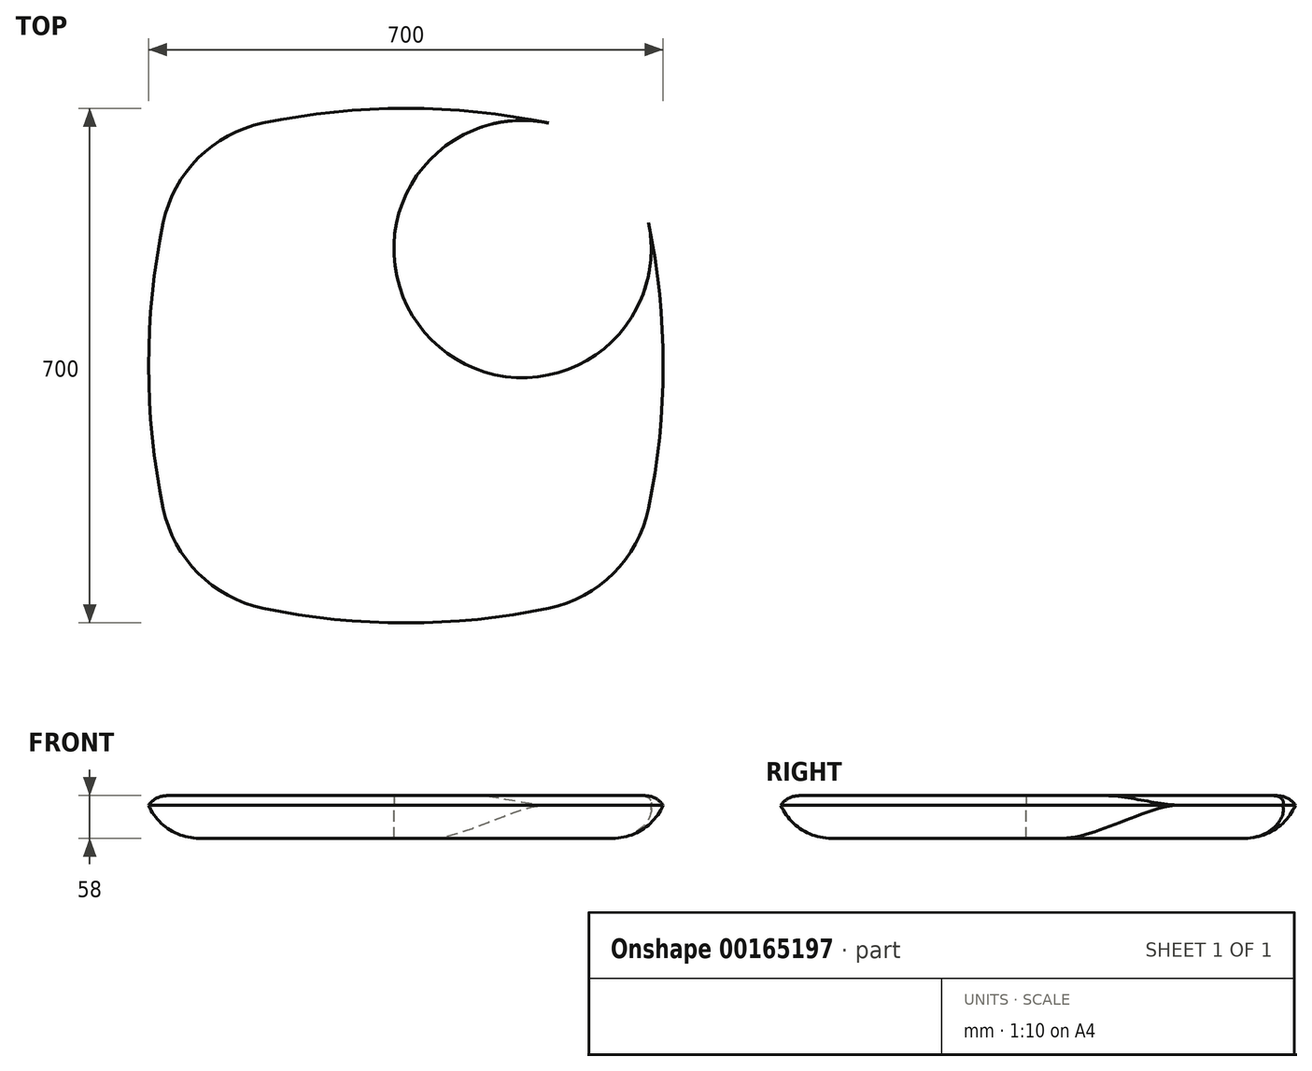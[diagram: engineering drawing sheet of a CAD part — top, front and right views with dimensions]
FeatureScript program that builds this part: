
annotation { "Feature Type Name" : "Feature", "Feature Type Description" : "" }
export const myFeature = defineFeature(function(context is Context, id is Id, definition is map)
    precondition{}
    {
        {
            var Q0;
            Q0=qCreatedBy(makeId("Top.planeOp"),FACE);
            var sketch = newSketch(context, id + "F0", { "sketchPlane" : qUnion([Q0])});
            skLineSegment(sketch, "E0.bottom", {"start": v(301.28, -301.28) * mm, "end": v(-301.28, -301.28) * mm, "construction": true});
            skLineSegment(sketch, "E0.top", {"start": v(301.28, 301.28) * mm, "end": v(-301.28, 301.28) * mm, "construction": true});
            skLineSegment(sketch, "E0.left", {"start": v(301.28, -301.28) * mm, "end": v(301.28, 301.28) * mm, "construction": true});
            skLineSegment(sketch, "E0.right", {"start": v(-301.28, -301.28) * mm, "end": v(-301.28, 301.28) * mm, "construction": true});
            skPoint(sketch, "E0.middle", {"position": v(0, 0) * mm});
            skArc(sketch, "E1", {"start": v(301.28, 301.28) * mm, "mid": v(0, 350) * mm, "end": v(-301.28, 301.28) * mm});
            skArc(sketch, "E2", {"start": v(-301.28, 301.28) * mm, "mid": v(-350, 0) * mm, "end": v(-301.28, -301.28) * mm});
            skArc(sketch, "E3", {"start": v(-301.28, -301.28) * mm, "mid": v(0, -350) * mm, "end": v(301.28, -301.28) * mm});
            skArc(sketch, "E4", {"start": v(301.28, -301.28) * mm, "mid": v(350, 0) * mm, "end": v(301.28, 301.28) * mm});
            skCircle(sketch, "E5", {"center": v(-158.7, -158.7) * mm, "radius": 175 * mm});
            skLineSegment(sketch, "E6", {"start": v(-301.28, 301.28) * mm, "end": v(301.28, -301.28) * mm, "construction": true});
            skLineSegment(sketch, "E7", {"start": v(-282.21, 0) * mm, "end": v(273.2, 0) * mm, "construction": true});
            skCircle(sketch, "E8.MirrorC", {"center": v(158.7, 158.7) * mm, "radius": 175 * mm});
            skCircle(sketch, "E9.MirrorC", {"center": v(-158.7, 158.7) * mm, "radius": 175 * mm});
            skCircle(sketch, "E10.MirrorC", {"center": v(158.7, -158.7) * mm, "radius": 175 * mm});
            skSolve(sketch);
        }
        {
            var Q0;
            {var subQ0=sQuery(id+"F0.wireOp",EDGE,"E5");var subQ1=makeQuery(id+"F0.imprint","INTERSECT",VERTEX,{"derivedFrom":[sQuery(id+"F0.wireOp",EDGE,"E2"),subQ0]});Q0=makeQuery(id+"F0.imprint","IMPRINT",FACE,{"disambiguationData":[TD([[makeQuery(id+"F0.imprint","IMPRINT",EDGE,{"disambiguationData":[TD([[subQ1,-1.0]])],"derivedFrom":subQ0}),1.0]])]});}
            var Q1;
            {var subQ3=sQuery(id+"F0.wireOp",EDGE,"E8.MirrorC");var subQ13=sQuery(id+"F0.wireOp",EDGE,"E1");var subQ14=makeQuery(id+"F0.imprint","INTERSECT",VERTEX,{"derivedFrom":[subQ13,subQ3]});Q1=makeQuery(id+"F0.imprint","IMPRINT",FACE,{"disambiguationData":[TD([[makeQuery(id+"F0.imprint","IMPRINT",EDGE,{"disambiguationData":[TD([[subQ14,-1.0]])],"derivedFrom":subQ13}),1.0]])]});}
            var Q2;
            {var subQ0=sQuery(id+"F0.wireOp",EDGE,"E10.MirrorC");var subQ1=makeQuery(id+"F0.imprint","INTERSECT",VERTEX,{"derivedFrom":[sQuery(id+"F0.wireOp",EDGE,"E3"),subQ0]});Q2=makeQuery(id+"F0.imprint","IMPRINT",FACE,{"disambiguationData":[TD([[makeQuery(id+"F0.imprint","IMPRINT",EDGE,{"disambiguationData":[TD([[subQ1,-1.0]])],"derivedFrom":subQ0}),1.0]])]});}
            var Q3;
            {var subQ0=sQuery(id+"F0.wireOp",EDGE,"E5");var subQ1=sQuery(id+"F0.wireOp",EDGE,"E3");var subQ2=makeQuery(id+"F0.imprint","INTERSECT",VERTEX,{"derivedFrom":[subQ1,subQ0]});Q3=makeQuery(id+"F0.imprint","IMPRINT",FACE,{"disambiguationData":[TD([[makeQuery(id+"F0.imprint","IMPRINT",EDGE,{"disambiguationData":[TD([[subQ2,-1.0]])],"derivedFrom":subQ1}),1.0]])]});}
            var Q4;
            {var subQ0=sQuery(id+"F0.wireOp",EDGE,"E9.MirrorC");var subQ1=sQuery(id+"F0.wireOp",EDGE,"E2");var subQ2=makeQuery(id+"F0.imprint","INTERSECT",VERTEX,{"derivedFrom":[subQ1,subQ0]});Q4=makeQuery(id+"F0.imprint","IMPRINT",FACE,{"disambiguationData":[TD([[makeQuery(id+"F0.imprint","IMPRINT",EDGE,{"disambiguationData":[TD([[subQ2,-1.0]])],"derivedFrom":subQ1}),1.0]])]});}
            var Q5;
            {var subQ0=sQuery(id+"F0.wireOp",EDGE,"E9.MirrorC");var subQ1=sQuery(id+"F0.wireOp",EDGE,"E5");var subQ2=makeQuery(id+"F0.imprint","INTERSECT",VERTEX,{"disambiguationData":[OD(0.0)],"derivedFrom":[subQ1,subQ0]});Q5=makeQuery(id+"F0.imprint","IMPRINT",FACE,{"disambiguationData":[TD([[makeQuery(id+"F0.imprint","IMPRINT",EDGE,{"disambiguationData":[TD([[subQ2,-1.0]])],"derivedFrom":subQ1}),1.0]])]});}
            var Q6;
            {var subQ0=sQuery(id+"F0.wireOp",EDGE,"E9.MirrorC");var subQ2=sQuery(id+"F0.wireOp",EDGE,"E5");var subQ4=makeQuery(id+"F0.imprint","INTERSECT",VERTEX,{"disambiguationData":[OD(0.0)],"derivedFrom":[subQ2,subQ0]});Q6=makeQuery(id+"F0.imprint","IMPRINT",FACE,{"disambiguationData":[TD([[makeQuery(id+"F0.imprint","IMPRINT",EDGE,{"disambiguationData":[TD([[subQ4,-1.0]])],"derivedFrom":subQ2}),-1.0]])]});}
            var Q7;
            {var subQ0=sQuery(id+"F0.wireOp",EDGE,"E9.MirrorC");var subQ1=sQuery(id+"F0.wireOp",EDGE,"E5");var subQ2=makeQuery(id+"F0.imprint","INTERSECT",VERTEX,{"disambiguationData":[OD(0.0)],"derivedFrom":[subQ1,subQ0]});Q7=makeQuery(id+"F0.imprint","IMPRINT",FACE,{"disambiguationData":[TD([[makeQuery(id+"F0.imprint","IMPRINT",EDGE,{"disambiguationData":[TD([[subQ2,1.0]])],"derivedFrom":subQ1}),-1.0]])]});}
            var Q8;
            {var subQ0=sQuery(id+"F0.wireOp",EDGE,"E8.MirrorC");var subQ4=sQuery(id+"F0.wireOp",EDGE,"E9.MirrorC");var subQ5=makeQuery(id+"F0.imprint","INTERSECT",VERTEX,{"disambiguationData":[OD(0.0)],"derivedFrom":[subQ0,subQ4]});Q8=makeQuery(id+"F0.imprint","IMPRINT",FACE,{"disambiguationData":[TD([[makeQuery(id+"F0.imprint","IMPRINT",EDGE,{"disambiguationData":[TD([[subQ5,1.0]])],"derivedFrom":subQ0}),-1.0]])]});}
            var Q9;
            {var subQ0=sQuery(id+"F0.wireOp",EDGE,"E10.MirrorC");var subQ1=sQuery(id+"F0.wireOp",EDGE,"E8.MirrorC");var subQ2=makeQuery(id+"F0.imprint","INTERSECT",VERTEX,{"disambiguationData":[OD(0.0)],"derivedFrom":[subQ1,subQ0]});Q9=makeQuery(id+"F0.imprint","IMPRINT",FACE,{"disambiguationData":[TD([[makeQuery(id+"F0.imprint","IMPRINT",EDGE,{"disambiguationData":[TD([[subQ2,1.0]])],"derivedFrom":subQ1}),-1.0]])]});}
            var Q10;
            {var subQ0=sQuery(id+"F0.wireOp",EDGE,"E10.MirrorC");var subQ1=sQuery(id+"F0.wireOp",EDGE,"E4");var subQ2=makeQuery(id+"F0.imprint","INTERSECT",VERTEX,{"derivedFrom":[subQ1,subQ0]});Q10=makeQuery(id+"F0.imprint","IMPRINT",FACE,{"disambiguationData":[TD([[makeQuery(id+"F0.imprint","IMPRINT",EDGE,{"disambiguationData":[TD([[subQ2,-1.0]])],"derivedFrom":subQ1}),1.0]])]});}
            var Q11;
            {var subQ0=sQuery(id+"F0.wireOp",EDGE,"E10.MirrorC");var subQ1=sQuery(id+"F0.wireOp",EDGE,"E5");var subQ2=makeQuery(id+"F0.imprint","INTERSECT",VERTEX,{"disambiguationData":[OD(0.0)],"derivedFrom":[subQ1,subQ0]});Q11=makeQuery(id+"F0.imprint","IMPRINT",FACE,{"disambiguationData":[TD([[makeQuery(id+"F0.imprint","IMPRINT",EDGE,{"disambiguationData":[TD([[subQ2,1.0]])],"derivedFrom":subQ1}),1.0]])]});}
            var Q12;
            {var subQ0=sQuery(id+"F0.wireOp",EDGE,"E9.MirrorC");var subQ1=sQuery(id+"F0.wireOp",EDGE,"E8.MirrorC");var subQ2=makeQuery(id+"F0.imprint","INTERSECT",VERTEX,{"disambiguationData":[OD(0.0)],"derivedFrom":[subQ1,subQ0]});Q12=makeQuery(id+"F0.imprint","IMPRINT",FACE,{"disambiguationData":[TD([[makeQuery(id+"F0.imprint","IMPRINT",EDGE,{"disambiguationData":[TD([[subQ2,-1.0]])],"derivedFrom":subQ1}),-1.0]])]});}
            extrude(context, id + "F1", {"entities" : qUnion([Q0, Q1, Q2, Q3, Q4, Q5, Q6, Q7, Q8, Q9, Q10, Q11, Q12]), "depth" : 13 * mm});
        }
        {
            var Q0;
            Q0=makeQuery(id+"F1.opExtrude","CAP_EDGE",EDGE,{"disambiguationData":[OSD([sQuery(id+"F0.wireOp",EDGE,"E3")])],"isStart":false});
            fillet(context, id + "F2", {"entities" : qUnion([Q0]), "radius" : 30.5 * mm, "tangentPropagation" : true, "allowEdgeOverflow" : false});
        }
        {
            var Q0;
            Q0=makeQuery(id+"F1.opExtrude","CAP_FACE",FACE,{"disambiguationData":[OSD([sQuery(id+"F0.wireOp",EDGE,"E1"),sQuery(id+"F0.wireOp",EDGE,"E2"),sQuery(id+"F0.wireOp",EDGE,"E3"),sQuery(id+"F0.wireOp",EDGE,"E4"),sQuery(id+"F0.wireOp",EDGE,"E5"),sQuery(id+"F0.wireOp",EDGE,"E8.MirrorC"),sQuery(id+"F0.wireOp",EDGE,"E9.MirrorC"),sQuery(id+"F0.wireOp",EDGE,"E10.MirrorC")])],"isStart":true});
            extrude(context, id + "F3", {"entities" : qUnion([Q0]), "depth" : 45 * mm});
        }
        {
            var Q0;
            {var subQ0=sQuery(id+"F0.wireOp",EDGE,"E10.MirrorC");var subQ1=sQuery(id+"F0.wireOp",EDGE,"E9.MirrorC");var subQ2=sQuery(id+"F0.wireOp",EDGE,"E8.MirrorC");var subQ3=sQuery(id+"F0.wireOp",EDGE,"E5");var subQ4=sQuery(id+"F0.wireOp",EDGE,"E4");var subQ5=sQuery(id+"F0.wireOp",EDGE,"E3");var subQ6=sQuery(id+"F0.wireOp",EDGE,"E2");var subQ7=sQuery(id+"F0.wireOp",EDGE,"E1");Q0=makeQuery(id+"F3.opExtrude","CAP_EDGE",EDGE,{"disambiguationData":[OSD([subQ7,subQ6,subQ5,subQ4,subQ3,subQ2,subQ1,subQ0]),TDD([makeQuery(id+"F2.opFillet","BLEND_EDGE",EDGE,{"blendedFrom":[makeQuery(id+"F1.opExtrude","CAP_EDGE",EDGE,{"disambiguationData":[OSD([subQ4])],"isStart":false}),makeQuery(id+"F1.opExtrude","CAP_FACE",FACE,{"disambiguationData":[OSD([subQ7,subQ6,subQ5,subQ4,subQ3,subQ2,subQ1,subQ0])],"isStart":true})],"blendedInto":[makeQuery(id+"F1.opExtrude","CAP_FACE",FACE,{"disambiguationData":[OSD([subQ7,subQ6,subQ5,subQ4,subQ3,subQ2,subQ1,subQ0])],"isStart":true})]})])],"isStart":false});}
            fillet(context, id + "F4", {"entities" : qUnion([Q0]), "radius" : 75 * mm, "tangentPropagation" : true, "allowEdgeOverflow" : false});
        }
    });
